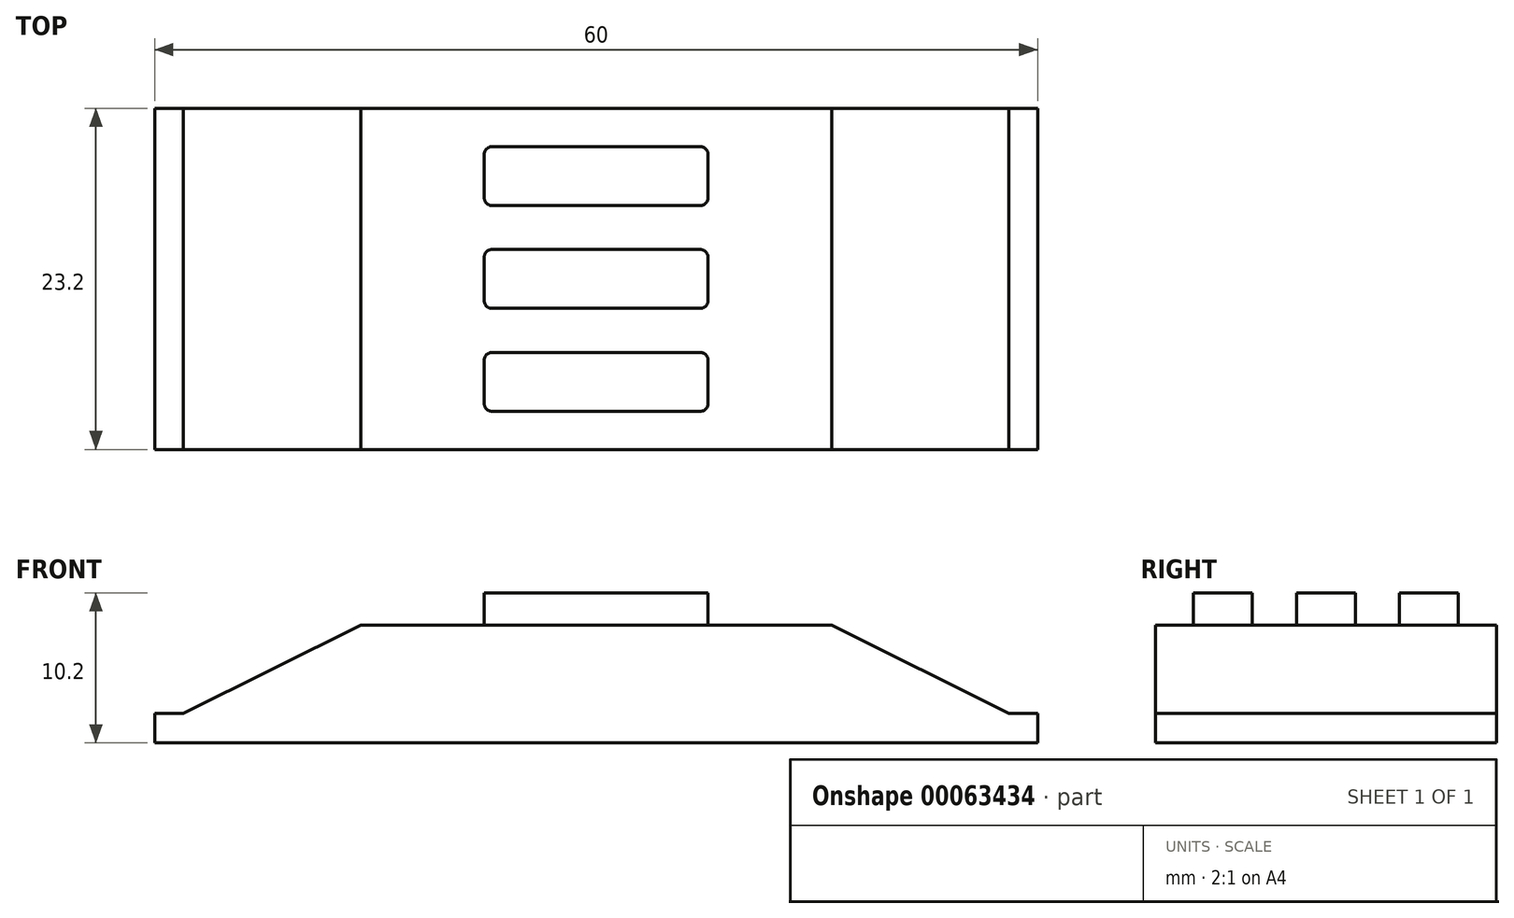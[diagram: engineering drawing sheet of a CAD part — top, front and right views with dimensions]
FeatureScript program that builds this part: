
annotation { "Feature Type Name" : "Feature", "Feature Type Description" : "" }
export const myFeature = defineFeature(function(context is Context, id is Id, definition is map)
    precondition{}
    {
        {
            var Q0;
            Q0=qCreatedBy(makeId("Top.planeOp"),FACE);
            var sketch = newSketch(context, id + "F0", { "sketchPlane" : qUnion([Q0])});
            skLineSegment(sketch, "E0.bottom", {"start": v(0, 0) * mm, "end": v(60, 0) * mm});
            skLineSegment(sketch, "E0.top", {"start": v(0, 23.2) * mm, "end": v(60, 23.2) * mm});
            skLineSegment(sketch, "E0.left", {"start": v(0, 0) * mm, "end": v(0, 23.2) * mm});
            skLineSegment(sketch, "E0.right", {"start": v(60, 0) * mm, "end": v(60, 23.2) * mm});
            skSolve(sketch);
        }
        {
            var Q0;
            Q0=makeQuery(id+"F0.imprint","IMPRINT",FACE,{"disambiguationData":[TD([[makeQuery(id+"F0.imprint","IMPRINT",EDGE,{"derivedFrom":sQuery(id+"F0.wireOp",EDGE,"E0.bottom")}),1.0]])]});
            extrude(context, id + "F1", {"entities" : qUnion([Q0]), "depth" : 2 * mm});
        }
        {
            var Q0;
            Q0=makeQuery(id+"F1.opExtrude","SWEPT_FACE",FACE,{"disambiguationData":[OSD([sQuery(id+"F0.wireOp",EDGE,"E0.top")])]});
            var sketch = newSketch(context, id + "F2", { "sketchPlane" : qUnion([Q0])});
            skLineSegment(sketch, "E1", {"start": v(-30, 0) * mm, "end": v(-30, 6.92) * mm, "construction": true});
            skLineSegment(sketch, "E2", {"start": v(-14, 8) * mm, "end": v(-1.95, 2) * mm});
            skLineSegment(sketch, "E3.MirrorCS", {"start": v(-46, 8) * mm, "end": v(-58.05, 2) * mm});
            skLineSegment(sketch, "E4", {"start": v(-1.95, 2) * mm, "end": v(-58.05, 2) * mm});
            skLineSegment(sketch, "E5", {"start": v(-46, 8) * mm, "end": v(-14, 8) * mm});
            skSolve(sketch);
        }
        {
            var Q0;
            Q0=makeQuery(id+"F2.imprint","IMPRINT",FACE,{"disambiguationData":[TD([[makeQuery(id+"F2.imprint","IMPRINT",EDGE,{"derivedFrom":sQuery(id+"F2.wireOp",EDGE,"E2")}),-1.0]])]});
            var Q1;
            Q1=makeQuery(id+"F1.opExtrude","SWEPT_FACE",FACE,{"disambiguationData":[OSD([sQuery(id+"F0.wireOp",EDGE,"E0.bottom")])]});
            extrude(context, id + "F3", {"entities" : qUnion([Q0]), "operationType" : NewBodyOperationType.ADD, "endBound" : BoundingType.UP_TO_SURFACE, "oppositeDirection" : true, "endBoundEntityFace" : qUnion([Q1]), "depth" : 30 * mm});
        }
        {
            var Q0;
            Q0=makeQuery(id+"F3.opExtrude","SWEPT_FACE",FACE,{"disambiguationData":[OSD([sQuery(id+"F2.wireOp",EDGE,"E5")])]});
            var sketch = newSketch(context, id + "F4", { "sketchPlane" : qUnion([Q0]), "disableImprinting" : false});
            skLineSegment(sketch, "E6", {"start": v(30, 23.2) * mm, "end": v(30, 0) * mm, "construction": true});
            skLineSegment(sketch, "E7", {"start": v(14, 11.6) * mm, "end": v(46, 11.6) * mm, "construction": true});
            skLineSegment(sketch, "E8", {"start": v(22.4, 23.2) * mm, "end": v(22.4, 0) * mm, "construction": true});
            skLineSegment(sketch, "E9.MirrorCS", {"start": v(37.6, 23.2) * mm, "end": v(37.6, 0) * mm, "construction": true});
            skLineSegment(sketch, "E10.bottom", {"start": v(22.4, 20.6) * mm, "end": v(37.6, 20.6) * mm});
            skLineSegment(sketch, "E10.top", {"start": v(22.4, 16.6) * mm, "end": v(37.6, 16.6) * mm});
            skLineSegment(sketch, "E10.left", {"start": v(22.4, 20.6) * mm, "end": v(22.4, 16.6) * mm});
            skLineSegment(sketch, "E10.right", {"start": v(37.6, 20.6) * mm, "end": v(37.6, 16.6) * mm});
            skLineSegment(sketch, "E11", {"start": v(22.4, 11.6) * mm, "end": v(22.4, 13.6) * mm});
            skLineSegment(sketch, "E12", {"start": v(22.4, 13.6) * mm, "end": v(37.6, 13.6) * mm});
            skLineSegment(sketch, "E13", {"start": v(37.6, 13.6) * mm, "end": v(37.6, 11.6) * mm});
            skLineSegment(sketch, "E14.MirrorCS", {"start": v(22.4, 6.6) * mm, "end": v(37.6, 6.6) * mm});
            skLineSegment(sketch, "E15.MirrorCS", {"start": v(37.6, 2.6) * mm, "end": v(37.6, 6.6) * mm});
            skLineSegment(sketch, "E16.MirrorCS", {"start": v(22.4, 2.6) * mm, "end": v(37.6, 2.6) * mm});
            skLineSegment(sketch, "E17.MirrorCS", {"start": v(22.4, 2.6) * mm, "end": v(22.4, 6.6) * mm});
            skLineSegment(sketch, "E18.MirrorCS", {"start": v(37.6, 9.6) * mm, "end": v(37.6, 11.6) * mm});
            skLineSegment(sketch, "E19.MirrorCS", {"start": v(22.4, 11.6) * mm, "end": v(22.4, 9.6) * mm});
            skLineSegment(sketch, "E20.MirrorCS", {"start": v(22.4, 9.6) * mm, "end": v(37.6, 9.6) * mm});
            skSolve(sketch);
        }
        {
            var Q0;
            Q0=makeQuery(id+"F4.imprint","IMPRINT",FACE,{"disambiguationData":[TD([[makeQuery(id+"F4.imprint","IMPRINT",EDGE,{"derivedFrom":sQuery(id+"F4.wireOp",EDGE,"E10.bottom")}),-1.0]])]});
            var Q1;
            Q1=makeQuery(id+"F4.imprint","IMPRINT",FACE,{"disambiguationData":[TD([[makeQuery(id+"F4.imprint","IMPRINT",EDGE,{"derivedFrom":sQuery(id+"F4.wireOp",EDGE,"E11")}),-1.0]])]});
            var Q2;
            Q2=makeQuery(id+"F4.imprint","IMPRINT",FACE,{"disambiguationData":[TD([[makeQuery(id+"F4.imprint","IMPRINT",EDGE,{"derivedFrom":sQuery(id+"F4.wireOp",EDGE,"E14.MirrorCS")}),-1.0]])]});
            extrude(context, id + "F5", {"entities" : qUnion([Q0, Q1, Q2]), "operationType" : NewBodyOperationType.ADD, "depth" : 2.2 * mm});
        }
        {
            var Q0;
            Q0=makeQuery(id+"F5.opExtrude","SWEPT_EDGE",EDGE,{"disambiguationData":[OSD([sQuery(id+"F4.wireOp",EDGE,"E10.top"),sQuery(id+"F4.wireOp",EDGE,"E10.left")])]});
            var Q1;
            Q1=makeQuery(id+"F5.opExtrude","SWEPT_EDGE",EDGE,{"disambiguationData":[OSD([sQuery(id+"F4.wireOp",EDGE,"E19.MirrorCS"),sQuery(id+"F4.wireOp",EDGE,"E20.MirrorCS")])]});
            var Q2;
            Q2=makeQuery(id+"F5.opExtrude","SWEPT_EDGE",EDGE,{"disambiguationData":[OSD([sQuery(id+"F4.wireOp",EDGE,"E16.MirrorCS"),sQuery(id+"F4.wireOp",EDGE,"E17.MirrorCS")])]});
            var Q3;
            Q3=makeQuery(id+"F5.opExtrude","SWEPT_EDGE",EDGE,{"disambiguationData":[OSD([sQuery(id+"F4.wireOp",EDGE,"E15.MirrorCS"),sQuery(id+"F4.wireOp",EDGE,"E16.MirrorCS")])]});
            var Q4;
            Q4=makeQuery(id+"F5.opExtrude","SWEPT_EDGE",EDGE,{"disambiguationData":[OSD([sQuery(id+"F4.wireOp",EDGE,"E18.MirrorCS"),sQuery(id+"F4.wireOp",EDGE,"E20.MirrorCS")])]});
            var Q5;
            Q5=makeQuery(id+"F5.opExtrude","SWEPT_EDGE",EDGE,{"disambiguationData":[OSD([sQuery(id+"F4.wireOp",EDGE,"E10.top"),sQuery(id+"F4.wireOp",EDGE,"E10.right")])]});
            var Q6;
            Q6=makeQuery(id+"F5.opExtrude","SWEPT_EDGE",EDGE,{"disambiguationData":[OSD([sQuery(id+"F4.wireOp",EDGE,"E14.MirrorCS"),sQuery(id+"F4.wireOp",EDGE,"E17.MirrorCS")])]});
            var Q7;
            Q7=makeQuery(id+"F5.opExtrude","SWEPT_EDGE",EDGE,{"disambiguationData":[OSD([sQuery(id+"F4.wireOp",EDGE,"E14.MirrorCS"),sQuery(id+"F4.wireOp",EDGE,"E15.MirrorCS")])]});
            var Q8;
            Q8=makeQuery(id+"F5.opExtrude","SWEPT_EDGE",EDGE,{"disambiguationData":[OSD([sQuery(id+"F4.wireOp",EDGE,"E12"),sQuery(id+"F4.wireOp",EDGE,"E13")])]});
            var Q9;
            Q9=makeQuery(id+"F5.opExtrude","SWEPT_EDGE",EDGE,{"disambiguationData":[OSD([sQuery(id+"F4.wireOp",EDGE,"E11"),sQuery(id+"F4.wireOp",EDGE,"E12")])]});
            var Q10;
            Q10=makeQuery(id+"F5.opExtrude","SWEPT_EDGE",EDGE,{"disambiguationData":[OSD([sQuery(id+"F4.wireOp",EDGE,"E10.bottom"),sQuery(id+"F4.wireOp",EDGE,"E10.left")])]});
            var Q11;
            Q11=makeQuery(id+"F5.opExtrude","SWEPT_EDGE",EDGE,{"disambiguationData":[OSD([sQuery(id+"F4.wireOp",EDGE,"E10.bottom"),sQuery(id+"F4.wireOp",EDGE,"E10.right")])]});
            fillet(context, id + "F6", {"entities" : qUnion([Q0, Q1, Q2, Q3, Q4, Q5, Q6, Q7, Q8, Q9, Q10, Q11]), "radius" : 0.5 * mm, "tangentPropagation" : true, "allowEdgeOverflow" : false});
        }
    });
